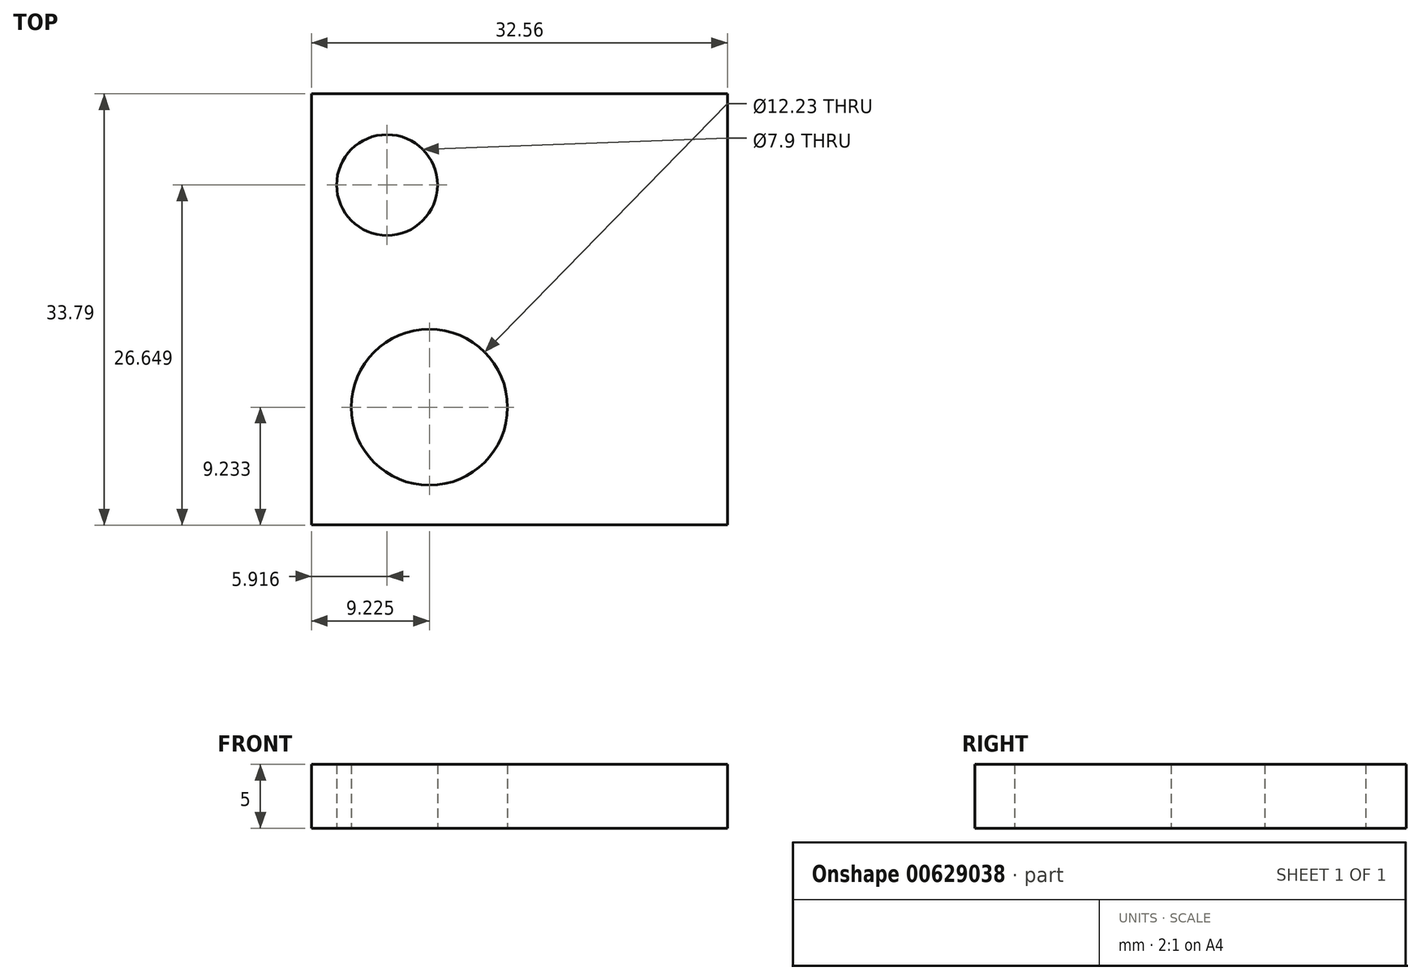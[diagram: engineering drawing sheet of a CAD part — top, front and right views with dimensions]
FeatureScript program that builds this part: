
annotation { "Feature Type Name" : "Feature", "Feature Type Description" : "" }
export const myFeature = defineFeature(function(context is Context, id is Id, definition is map)
    precondition{}
    {
        {
            var Q0;
            Q0=qCreatedBy(makeId("Top.planeOp"),FACE);
            var sketch = newSketch(context, id + "F0", { "sketchPlane" : qUnion([Q0])});
            skLineSegment(sketch, "E0.bottom", {"start": v(12.48, -38.44) * mm, "end": v(45.04, -38.44) * mm});
            skLineSegment(sketch, "E0.top", {"start": v(12.48, -4.65) * mm, "end": v(45.04, -4.65) * mm});
            skLineSegment(sketch, "E0.left", {"start": v(12.48, -38.44) * mm, "end": v(12.48, -4.65) * mm});
            skLineSegment(sketch, "E0.right", {"start": v(45.04, -38.44) * mm, "end": v(45.04, -4.65) * mm});
            skCircle(sketch, "E1", {"center": v(21.7, -29.2) * mm, "radius": 6.12 * mm});
            skCircle(sketch, "E2", {"center": v(18.4, -11.8) * mm, "radius": 3.95 * mm});
            skCircle(sketch, "E3", {"center": v(33.65, -21.1) * mm, "radius": 3.38 * mm});
            skSolve(sketch);
        }
        {
            var Q0;
            Q0=makeQuery(id+"F0.imprint","IMPRINT",FACE,{"disambiguationData":[TD([[makeQuery(id+"F0.imprint","IMPRINT",EDGE,{"derivedFrom":sQuery(id+"F0.wireOp",EDGE,"E0.bottom")}),1.0]])]});
            var Q1;
            Q1=makeQuery(id+"F0.imprint","IMPRINT",FACE,{"disambiguationData":[TD([[makeQuery(id+"F0.imprint","IMPRINT",EDGE,{"derivedFrom":sQuery(id+"F0.wireOp",EDGE,"E3")}),1.0]])]});
            extrude(context, id + "F1", {"entities" : qUnion([Q0, Q1]), "depth" : 5 * mm, "offsetDistance" : 25 * mm});
        }
        {
            var Q0;
            Q0=sQuery(id+"F0.wireOp",EDGE,"E0.right");
            cPlane(context, id + "F2", {"entities" : qUnion([Q0]), "cplaneType" : CPlaneType.LINE_ANGLE, "offset" : 25 * mm, "angle" : 15 * degree, "width" : 150 * mm, "height" : 150 * mm});
        }
    });
